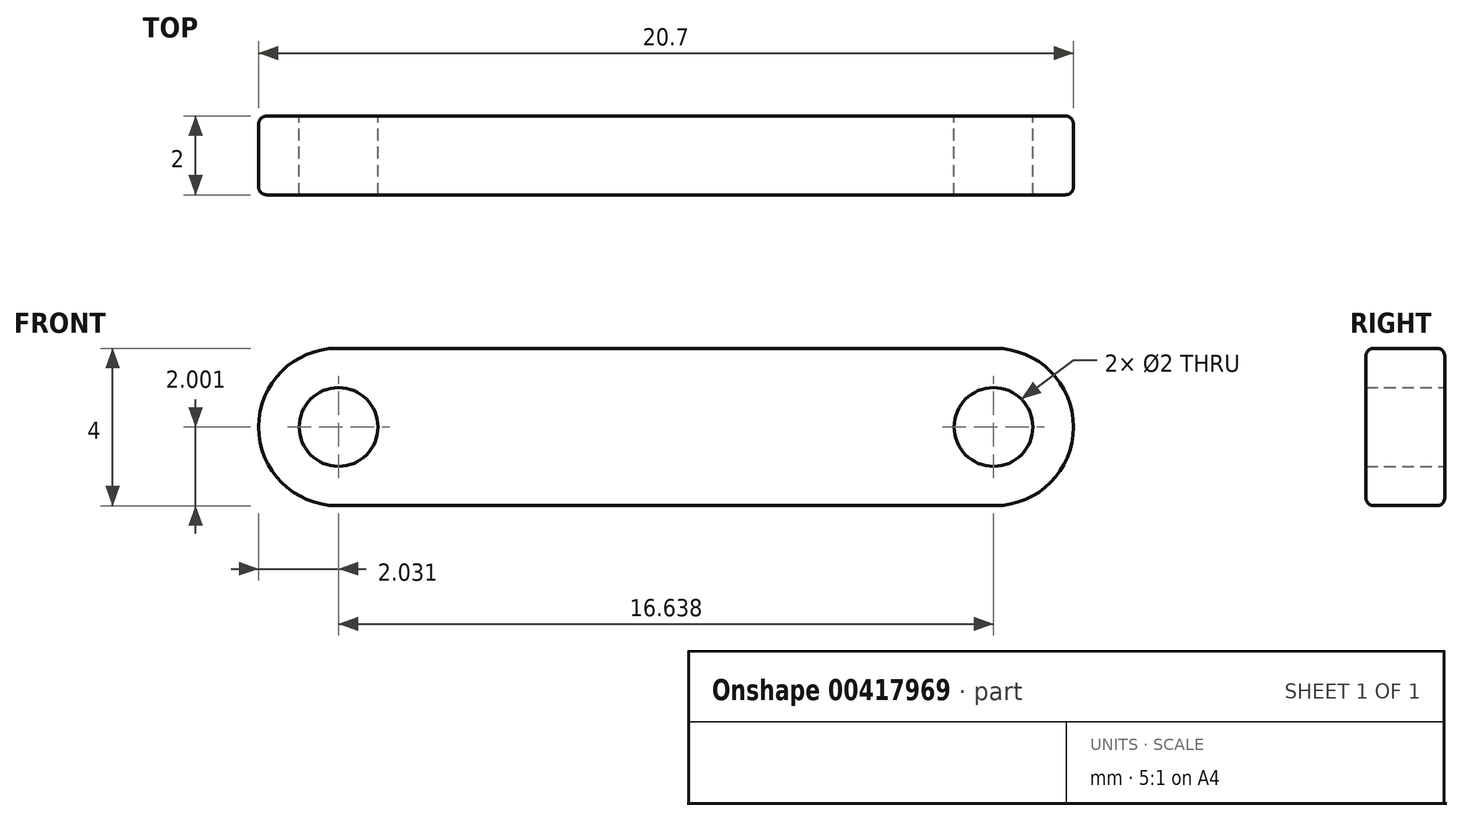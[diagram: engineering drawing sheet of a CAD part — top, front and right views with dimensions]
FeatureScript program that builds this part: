
annotation { "Feature Type Name" : "Feature", "Feature Type Description" : "" }
export const myFeature = defineFeature(function(context is Context, id is Id, definition is map)
    precondition{}
    {
        {
            var Q0;
            Q0=qCreatedBy(makeId("Front.planeOp"),FACE);
            var sketch = newSketch(context, id + "F0", { "sketchPlane" : qUnion([Q0])});
            skLineSegment(sketch, "E0.bottom", {"start": v(-10.6, 4.98) * mm, "end": v(10.1, 4.98) * mm});
            skLineSegment(sketch, "E0.top", {"start": v(-10.6, 0.98) * mm, "end": v(10.1, 0.98) * mm});
            skLineSegment(sketch, "E0.left", {"start": v(-10.6, 4.98) * mm, "end": v(-10.6, 0.98) * mm});
            skLineSegment(sketch, "E0.right", {"start": v(10.1, 4.98) * mm, "end": v(10.1, 0.98) * mm});
            skSolve(sketch);
        }
        {
            var Q0;
            Q0 = qSketchRegion(id + "F0", true);
            extrude(context, id + "F1", {"entities" : qUnion([Q0]), "depth" : 2 * mm});
        }
        {
            var Q0;
            Q0=makeQuery(id+"F1.opExtrude","SWEPT_EDGE",EDGE,{"disambiguationData":[OSD([sQuery(id+"F0.wireOp",EDGE,"E0.bottom"),sQuery(id+"F0.wireOp",EDGE,"E0.left")])]});
            var Q1;
            Q1=makeQuery(id+"F1.opExtrude","SWEPT_EDGE",EDGE,{"disambiguationData":[OSD([sQuery(id+"F0.wireOp",EDGE,"E0.top"),sQuery(id+"F0.wireOp",EDGE,"E0.left")])]});
            var Q2;
            Q2=makeQuery(id+"F1.opExtrude","SWEPT_EDGE",EDGE,{"disambiguationData":[OSD([sQuery(id+"F0.wireOp",EDGE,"E0.bottom"),sQuery(id+"F0.wireOp",EDGE,"E0.right")])]});
            var Q3;
            Q3=makeQuery(id+"F1.opExtrude","SWEPT_EDGE",EDGE,{"disambiguationData":[OSD([sQuery(id+"F0.wireOp",EDGE,"E0.top"),sQuery(id+"F0.wireOp",EDGE,"E0.right")])]});
            fillet(context, id + "F2", {"entities" : qUnion([Q0, Q1, Q2, Q3]), "radius" : 2 * mm, "tangentPropagation" : true, "allowEdgeOverflow" : false});
        }
        {
            var Q0;
            Q0=makeQuery(id+"F1.opExtrude","CAP_EDGE",EDGE,{"disambiguationData":[OSD([sQuery(id+"F0.wireOp",EDGE,"E0.bottom")])],"isStart":true});
            var Q1;
            Q1=makeQuery(id+"F1.opExtrude","CAP_EDGE",EDGE,{"disambiguationData":[OSD([sQuery(id+"F0.wireOp",EDGE,"E0.bottom")])],"isStart":false});
            fillet(context, id + "F3", {"entities" : qUnion([Q0, Q1]), "radius" : 0.2 * mm, "tangentPropagation" : true, "allowEdgeOverflow" : false});
        }
        {
            var Q0;
            Q0=makeQuery(id+"F1.opExtrude","CAP_FACE",FACE,{"disambiguationData":[OSD([sQuery(id+"F0.wireOp",EDGE,"E0.bottom"),sQuery(id+"F0.wireOp",EDGE,"E0.top"),sQuery(id+"F0.wireOp",EDGE,"E0.left"),sQuery(id+"F0.wireOp",EDGE,"E0.right")])],"isStart":true});
            var sketch = newSketch(context, id + "F4", { "sketchPlane" : qUnion([Q0])});
            skLineSegment(sketch, "E1", {"start": v(-11.99, 2.98) * mm, "end": v(13.46, 2.98) * mm, "construction": true});
            skPoint(sketch, "E1.startSnap0", {"position": v(-9.9, 2.98) * mm});
            skPoint(sketch, "E1.endSnap0", {"position": v(10.4, 2.98) * mm});
            skCircle(sketch, "E2", {"center": v(8.58, 2.98) * mm, "radius": 1 * mm});
            skCircle(sketch, "E3", {"center": v(-8.06, 2.98) * mm, "radius": 1 * mm});
            skSolve(sketch);
        }
        {
            var Q0;
            Q0 = qSketchRegion(id + "F4", true);
            extrude(context, id + "F5", {"entities" : qUnion([Q0]), "operationType" : NewBodyOperationType.REMOVE, "oppositeDirection" : true, "depth" : 25 * mm});
        }
    });
